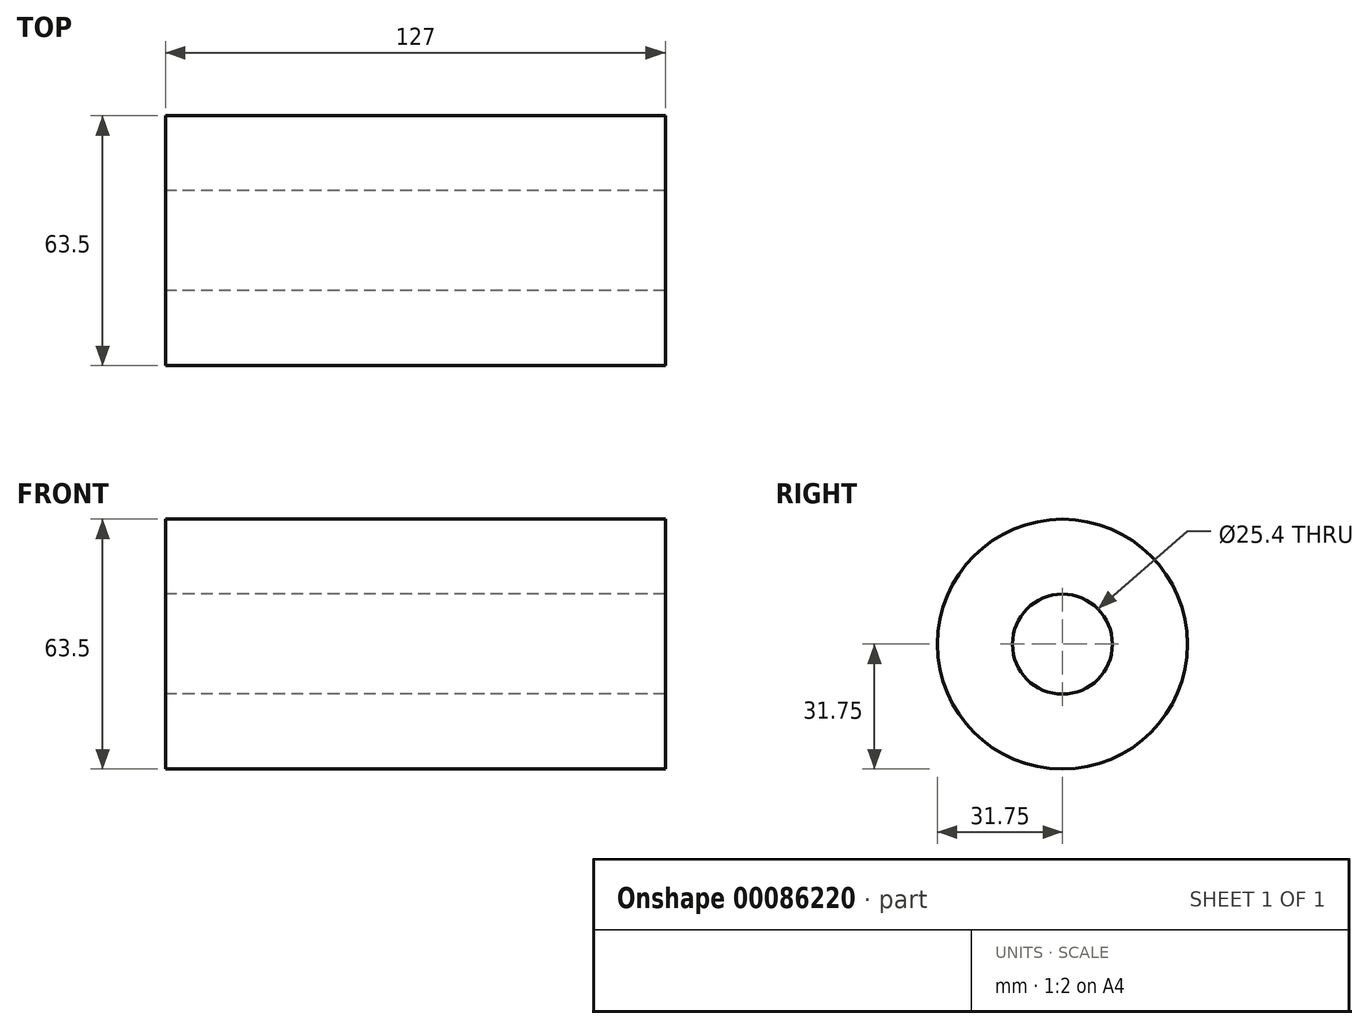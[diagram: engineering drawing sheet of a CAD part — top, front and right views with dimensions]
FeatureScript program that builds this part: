
annotation { "Feature Type Name" : "Feature", "Feature Type Description" : "" }
export const myFeature = defineFeature(function(context is Context, id is Id, definition is map)
    precondition{}
    {
        {
            var Q0;
            Q0=qCreatedBy(makeId("Front.planeOp"),FACE);
            var sketch = newSketch(context, id + "F0", { "sketchPlane" : qUnion([Q0])});
            skLineSegment(sketch, "E0.bottom", {"start": v(0, 12.7) * mm, "end": v(127, 12.7) * mm});
            skLineSegment(sketch, "E0.top", {"start": v(0, 31.75) * mm, "end": v(127, 31.75) * mm});
            skLineSegment(sketch, "E0.left", {"start": v(0, 12.7) * mm, "end": v(0, 31.75) * mm});
            skLineSegment(sketch, "E0.right", {"start": v(127, 12.7) * mm, "end": v(127, 31.75) * mm});
            skLineSegment(sketch, "E1", {"start": v(-124.66, 0) * mm, "end": v(116.97, 0) * mm, "construction": true});
            skSolve(sketch);
        }
        {
            var Q0;
            Q0=makeQuery(id+"F0.imprint","IMPRINT",FACE,{"disambiguationData":[TD([[makeQuery(id+"F0.imprint","IMPRINT",EDGE,{"derivedFrom":sQuery(id+"F0.wireOp",EDGE,"E0.bottom")}),1.0]])]});
            var Q1;
            Q1=sQuery(id+"F0.wireOp",EDGE,"E1");
            revolve(context, id + "F1", {"entities" : qUnion([Q0]), "axis" : qUnion([Q1]), "revolveType" : RevolveType.FULL});
        }
    });
